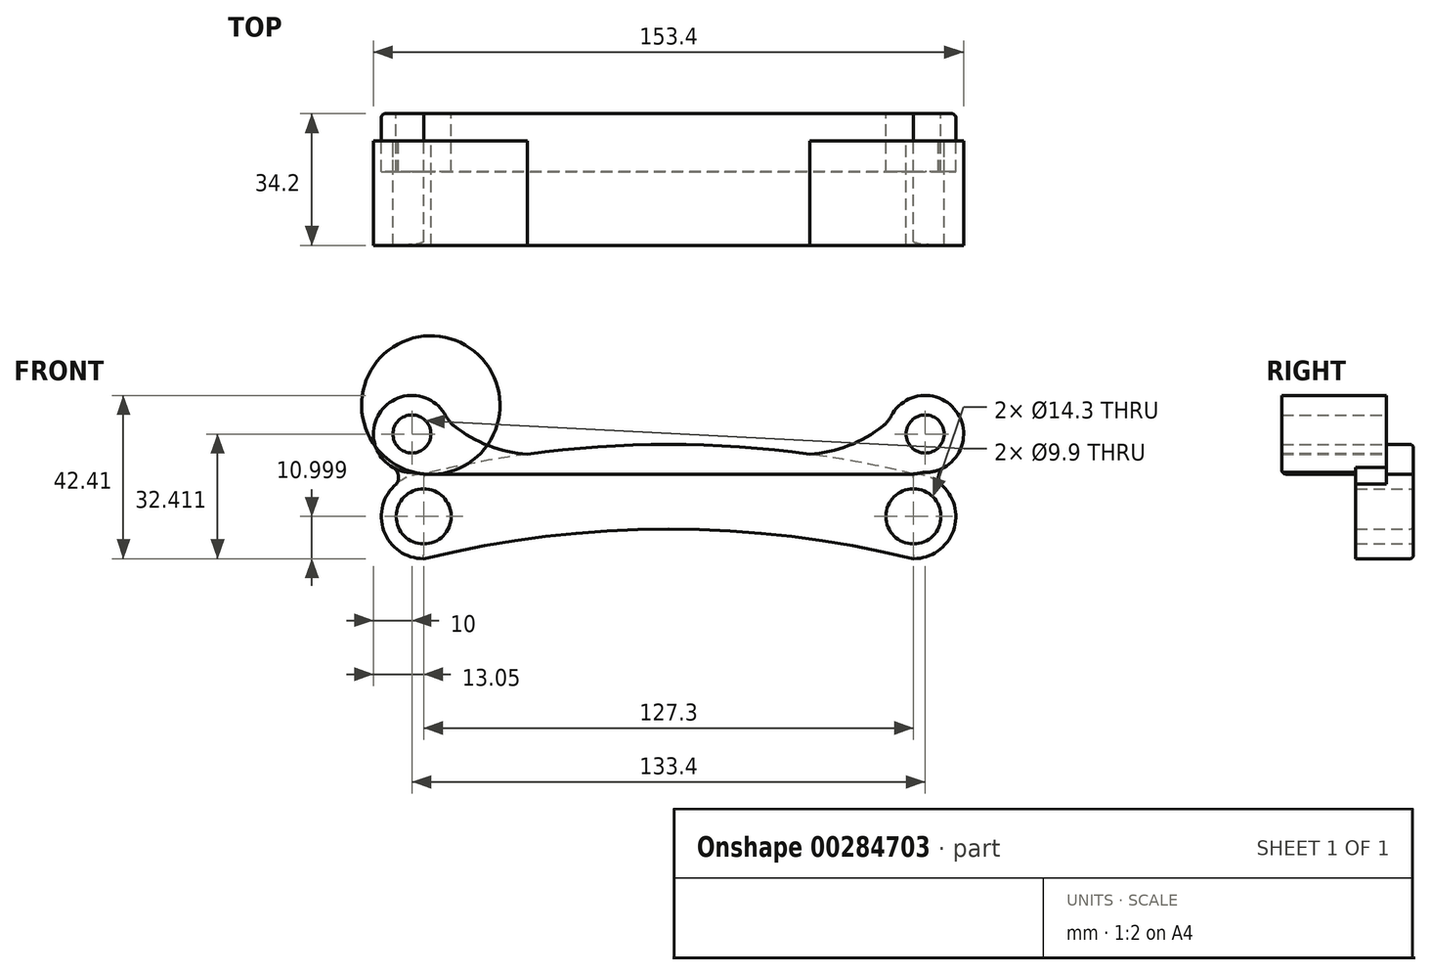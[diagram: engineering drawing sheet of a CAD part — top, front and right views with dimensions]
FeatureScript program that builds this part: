
annotation { "Feature Type Name" : "Feature", "Feature Type Description" : "" }
export const myFeature = defineFeature(function(context is Context, id is Id, definition is map)
    precondition{}
    {
        {
            var Q0;
            Q0=qCreatedBy(makeId("Front.planeOp"),FACE);
            var sketch = newSketch(context, id + "F0", { "sketchPlane" : qUnion([Q0])});
            skCircle(sketch, "E0", {"center": v(0, 0) * mm, "radius": 103 * mm, "construction": true});
            skCircle(sketch, "E1", {"center": v(0, 0) * mm, "radius": 122.2 * mm, "construction": true});
            skPoint(sketch, "E2", {"position": v(-63.65, 80.98) * mm});
            skPoint(sketch, "E3", {"position": v(63.65, 80.98) * mm});
            skPoint(sketch, "E4", {"position": v(-66.7, 102.4) * mm});
            skPoint(sketch, "E5", {"position": v(66.7, 102.4) * mm});
            skCircle(sketch, "E6", {"center": v(-66.7, 102.4) * mm, "radius": 4.95 * mm});
            skCircle(sketch, "E7", {"center": v(66.7, 102.4) * mm, "radius": 4.95 * mm});
            skCircle(sketch, "E8", {"center": v(63.65, 80.98) * mm, "radius": 7.15 * mm});
            skCircle(sketch, "E9", {"center": v(-63.65, 80.98) * mm, "radius": 7.15 * mm});
            skLineSegment(sketch, "E10", {"start": v(-66.7, 102.4) * mm, "end": v(-66.7, 80.98) * mm, "construction": true});
            skPoint(sketch, "E11", {"position": v(0, 91.69) * mm});
            skPoint(sketch, "E11.positionSnap0", {"position": v(-66.7, 91.69) * mm});
            skPoint(sketch, "E12", {"position": v(-66.7, 114.19) * mm});
            skPoint(sketch, "E13", {"position": v(66.7, 114.19) * mm});
            skCircle(sketch, "E14", {"center": v(-63.65, 80.98) * mm, "radius": 11 * mm});
            skCircle(sketch, "E15", {"center": v(63.65, 80.98) * mm, "radius": 11 * mm});
            skCircle(sketch, "E16", {"center": v(-66.7, 102.4) * mm, "radius": 10 * mm});
            skCircle(sketch, "E17", {"center": v(66.7, 102.4) * mm, "radius": 10 * mm});
            skPoint(sketch, "E18", {"position": v(-63.65, 91.98) * mm});
            skPoint(sketch, "E19", {"position": v(63.65, 92.87) * mm});
            skPoint(sketch, "E20", {"position": v(63.65, 91.98) * mm});
            skPoint(sketch, "E21", {"position": v(0, 99.69) * mm});
            skArc(sketch, "E22", {"start": v(63.65, 91.98) * mm, "mid": v(0, 99.69) * mm, "end": v(-63.65, 91.98) * mm});
            skPoint(sketch, "E23", {"position": v(0, 77.69) * mm});
            skPoint(sketch, "E24", {"position": v(-63.65, 69.98) * mm});
            skPoint(sketch, "E25", {"position": v(63.65, 69.98) * mm});
            skArc(sketch, "E26", {"start": v(63.65, 69.98) * mm, "mid": v(0, 77.69) * mm, "end": v(-63.65, 69.98) * mm});
            skPoint(sketch, "E27", {"position": v(-36.7, 97.15) * mm});
            skLineSegment(sketch, "E28", {"start": v(-66.7, 102.4) * mm, "end": v(-57.3, 105.81) * mm, "construction": true});
            skArc(sketch, "E29", {"start": v(-57.3, 105.81) * mm, "mid": v(-47.73, 99.74) * mm, "end": v(-36.7, 97.15) * mm});
            skLineSegment(sketch, "E30", {"start": v(-66.7, 102.4) * mm, "end": v(-76.1, 98.97) * mm});
            skArc(sketch, "E31", {"start": v(-76.1, 98.97) * mm, "mid": v(-70.6, 94.19) * mm, "end": v(-63.65, 91.98) * mm});
            skLineSegment(sketch, "E32", {"start": v(0, 91.69) * mm, "end": v(0, 77.69) * mm, "construction": true});
            skArc(sketch, "E33.MirrorCS", {"start": v(57.3, 105.81) * mm, "mid": v(47.73, 99.74) * mm, "end": v(36.7, 97.15) * mm});
            skArc(sketch, "E34.MirrorCS", {"start": v(76.1, 98.97) * mm, "mid": v(70.6, 94.19) * mm, "end": v(63.65, 91.98) * mm});
            skLineSegment(sketch, "E35", {"start": v(-63.65, 91.98) * mm, "end": v(63.65, 91.98) * mm});
            skArc(sketch, "E36", {"start": v(-70.6, 89.5) * mm, "mid": v(-70.99, 92.05) * mm, "end": v(-72.42, 94.19) * mm});
            skPoint(sketch, "E36.startSnap0", {"position": v(-70.6, 94.19) * mm});
            skPoint(sketch, "E36.endSnap0", {"position": v(-70.6, 94.19) * mm});
            skArc(sketch, "E37.MirrorCS", {"start": v(70.6, 89.5) * mm, "mid": v(70.99, 92.05) * mm, "end": v(72.42, 94.19) * mm});
            skSolve(sketch);
        }
        {
            var Q0;
            Q0=makeQuery(id+"F0.imprint","IMPRINT",FACE,{"disambiguationData":[TD([[makeQuery(id+"F0.imprint","IMPRINT",EDGE,{"derivedFrom":sQuery(id+"F0.wireOp",EDGE,"E6")}),-1.0]])]});
            var Q1;
            {var subQ0=sQuery(id+"F0.wireOp",EDGE,"E29");var subQ1=sQuery(id+"F0.wireOp",EDGE,"E16");var subQ2=makeQuery(id+"F0.imprint","INTERSECT",VERTEX,{"disambiguationData":[OD(1.0)],"derivedFrom":[subQ1,subQ0]});Q1=makeQuery(id+"F0.imprint","IMPRINT",FACE,{"disambiguationData":[TD([[makeQuery(id+"F0.imprint","IMPRINT",EDGE,{"disambiguationData":[TD([[subQ2,1.0]])],"derivedFrom":subQ1}),-1.0]])]});}
            var Q2;
            {var subQ0=sQuery(id+"F0.wireOp",EDGE,"E33.MirrorCS");var subQ1=sQuery(id+"F0.wireOp",EDGE,"E17");var subQ2=makeQuery(id+"F0.imprint","INTERSECT",VERTEX,{"disambiguationData":[OD(1.0)],"derivedFrom":[subQ1,subQ0]});Q2=makeQuery(id+"F0.imprint","IMPRINT",FACE,{"disambiguationData":[TD([[makeQuery(id+"F0.imprint","IMPRINT",EDGE,{"disambiguationData":[TD([[subQ2,-1.0]])],"derivedFrom":subQ1}),-1.0]])]});}
            var Q3;
            {var subQ0=sQuery(id+"F0.wireOp",EDGE,"E35");Q3=makeQuery(id+"F0.imprint","IMPRINT",FACE,{"disambiguationData":[TD([[makeQuery(id+"F0.imprint","IMPRINT",EDGE,{"derivedFrom":subQ0}),1.0]])]});}
            var Q4;
            Q4=makeQuery(id+"F0.imprint","IMPRINT",FACE,{"disambiguationData":[TD([[makeQuery(id+"F0.imprint","IMPRINT",EDGE,{"derivedFrom":sQuery(id+"F0.wireOp",EDGE,"E7")}),-1.0]])]});
            var Q5;
            {var subQ0=sQuery(id+"F0.wireOp",EDGE,"E31");var subQ1=sQuery(id+"F0.wireOp",EDGE,"E16");var subQ2=makeQuery(id+"F0.imprint","INTERSECT",VERTEX,{"disambiguationData":[OD(0.0)],"derivedFrom":[subQ1,subQ0]});Q5=makeQuery(id+"F0.imprint","IMPRINT",FACE,{"disambiguationData":[TD([[makeQuery(id+"F0.imprint","IMPRINT",EDGE,{"disambiguationData":[TD([[subQ2,-1.0]])],"derivedFrom":subQ1}),1.0]])]});}
            var Q6;
            {var subQ0=sQuery(id+"F0.wireOp",EDGE,"E17");var subQ1=makeQuery(id+"F0.imprint","INTERSECT",VERTEX,{"derivedFrom":[subQ0,sQuery(id+"F0.wireOp",EDGE,"E37.MirrorCS")]});Q6=makeQuery(id+"F0.imprint","IMPRINT",FACE,{"disambiguationData":[TD([[makeQuery(id+"F0.imprint","IMPRINT",EDGE,{"disambiguationData":[TD([[subQ1,1.0]])],"derivedFrom":subQ0}),1.0]])]});}
            extrude(context, id + "F1", {"entities" : qUnion([Q0, Q1, Q2, Q3, Q4, Q5, Q6]), "depth" : 24.2 * mm});
        }
        {
            var Q0;
            {var subQ0=sQuery(id+"F0.wireOp",EDGE,"E35");Q0=makeQuery(id+"F0.imprint","IMPRINT",FACE,{"disambiguationData":[TD([[makeQuery(id+"F0.imprint","IMPRINT",EDGE,{"derivedFrom":subQ0}),-1.0]])]});}
            var Q1;
            Q1=makeQuery(id+"F0.imprint","IMPRINT",FACE,{"disambiguationData":[TD([[makeQuery(id+"F0.imprint","IMPRINT",EDGE,{"derivedFrom":sQuery(id+"F0.wireOp",EDGE,"E9")}),-1.0]])]});
            var Q2;
            Q2=makeQuery(id+"F0.imprint","IMPRINT",FACE,{"disambiguationData":[TD([[makeQuery(id+"F0.imprint","IMPRINT",EDGE,{"derivedFrom":sQuery(id+"F0.wireOp",EDGE,"E8")}),-1.0]])]});
            var Q3;
            {var subQ0=sQuery(id+"F0.wireOp",EDGE,"E35");Q3=makeQuery(id+"F0.imprint","IMPRINT",FACE,{"disambiguationData":[TD([[makeQuery(id+"F0.imprint","IMPRINT",EDGE,{"derivedFrom":subQ0}),1.0]])]});}
            extrude(context, id + "F2", {"entities" : qUnion([Q0, Q1, Q2, Q3]), "operationType" : NewBodyOperationType.ADD, "endBound" : BoundingType.SYMMETRIC, "depth" : 20 * mm});
        }
        {
            var Q0;
            Q0=makeQuery(id+"F2.opExtrude","CAP_FACE",FACE,{"disambiguationData":[OSD([sQuery(id+"F0.wireOp",EDGE,"E8"),sQuery(id+"F0.wireOp",EDGE,"E9"),sQuery(id+"F0.wireOp",EDGE,"E14"),sQuery(id+"F0.wireOp",EDGE,"E15"),sQuery(id+"F0.wireOp",EDGE,"E22"),sQuery(id+"F0.wireOp",EDGE,"E26")])],"isStart":false});
            var sketch = newSketch(context, id + "F3", { "sketchPlane" : qUnion([Q0])});
            skArc(sketch, "E38.0", {"start": v(63.65, 69.98) * mm, "mid": v(0, 77.69) * mm, "end": v(-63.65, 69.98) * mm});
            skArc(sketch, "E39.0", {"start": v(-63.65, 91.98) * mm, "mid": v(-74.65, 80.98) * mm, "end": v(-63.65, 69.98) * mm});
            skLineSegment(sketch, "E40.0", {"start": v(-63.65, 91.98) * mm, "end": v(63.65, 91.98) * mm});
            skArc(sketch, "E41.0", {"start": v(63.65, 69.98) * mm, "mid": v(74.65, 80.98) * mm, "end": v(63.65, 91.98) * mm});
            skSolve(sketch);
        }
        {
            var Q0;
            Q0 = qSketchRegion(id + "F3", true);
            extrude(context, id + "F4", {"entities" : qUnion([Q0]), "operationType" : NewBodyOperationType.REMOVE, "oppositeDirection" : true, "depth" : 5 * mm});
        }
        {
            var Q0;
            {var subQ0=sQuery(id+"F0.wireOp",EDGE,"E29");var subQ1=sQuery(id+"F0.wireOp",EDGE,"E22");var subQ2=sQuery(id+"F0.wireOp",EDGE,"E16");var subQ3=sQuery(id+"F0.wireOp",EDGE,"E6");var subQ4=sQuery(id+"F0.wireOp",EDGE,"E31");Q0=makeQuery(id+"F2.boolean.opBoolean","SPLIT",FACE,{"disambiguationData":[TD([makeQuery(id+"F1.opExtrude","SWEPT_FACE",FACE,{"disambiguationData":[OSD([subQ3])]})])],"derivedFrom":makeQuery(id+"F1.opExtrude","CAP_FACE",FACE,{"disambiguationData":[OSD([subQ3,sQuery(id+"F0.wireOp",EDGE,"E7"),subQ2,sQuery(id+"F0.wireOp",EDGE,"E17"),subQ1,subQ0,subQ4,sQuery(id+"F0.wireOp",EDGE,"E33.MirrorCS"),sQuery(id+"F0.wireOp",EDGE,"E34.MirrorCS"),sQuery(id+"F0.wireOp",EDGE,"E35")])],"isStart":true})});}
            var sketch = newSketch(context, id + "F5", { "sketchPlane" : qUnion([Q0])});
            skArc(sketch, "E42.0", {"start": v(57.3, 105.81) * mm, "mid": v(47.73, 99.74) * mm, "end": v(36.7, 97.15) * mm});
            skArc(sketch, "E43.0", {"start": v(57.3, 105.81) * mm, "mid": v(75.06, 107.88) * mm, "end": v(66.1, 92.4) * mm});
            skArc(sketch, "E44.0", {"start": v(66.1, 92.4) * mm, "mid": v(64.88, 92.15) * mm, "end": v(63.65, 91.98) * mm});
            skCircle(sketch, "E45.0", {"center": v(66.7, 102.4) * mm, "radius": 4.95 * mm});
            skArc(sketch, "E46.0", {"start": v(-66.1, 92.4) * mm, "mid": v(-75.06, 107.88) * mm, "end": v(-57.3, 105.81) * mm});
            skArc(sketch, "E47.0", {"start": v(-57.3, 105.81) * mm, "mid": v(-47.73, 99.74) * mm, "end": v(-36.7, 97.15) * mm});
            skArc(sketch, "E48.0", {"start": v(-66.1, 92.4) * mm, "mid": v(-64.88, 92.15) * mm, "end": v(-63.65, 91.98) * mm});
            skArc(sketch, "E49.0", {"start": v(-36.7, 97.15) * mm, "mid": v(-50.24, 94.91) * mm, "end": v(-63.65, 91.98) * mm});
            skCircle(sketch, "E50.0", {"center": v(-66.7, 102.4) * mm, "radius": 4.95 * mm});
            skArc(sketch, "E51.0", {"start": v(63.65, 91.98) * mm, "mid": v(50.24, 94.91) * mm, "end": v(36.7, 97.15) * mm});
            skSolve(sketch);
        }
        {
            var Q0;
            Q0 = qSketchRegion(id + "F5", true);
            extrude(context, id + "F6", {"entities" : qUnion([Q0]), "operationType" : NewBodyOperationType.ADD, "depth" : 3 * mm});
        }
        {
            var Q0;
            Q0=makeQuery(id+"F1.opExtrude","CAP_EDGE",EDGE,{"disambiguationData":[OSD([sQuery(id+"F0.wireOp",EDGE,"E35")])],"isStart":false});
            var Q1;
            Q1=makeQuery(id+"F2.opExtrude","CAP_EDGE",EDGE,{"disambiguationData":[OSD([sQuery(id+"F0.wireOp",EDGE,"E22")])],"isStart":true});
            var Q2;
            Q2=makeQuery(id+"F2.opExtrude","CAP_EDGE",EDGE,{"disambiguationData":[OSD([sQuery(id+"F0.wireOp",EDGE,"E26")])],"isStart":true});
            var Q3;
            Q3=makeQuery(id+"F2.opExtrude","CAP_EDGE",EDGE,{"disambiguationData":[OSD([sQuery(id+"F0.wireOp",EDGE,"E14")])],"isStart":true});
            var Q4;
            Q4=makeQuery(id+"F2.opExtrude","CAP_EDGE",EDGE,{"disambiguationData":[OSD([sQuery(id+"F0.wireOp",EDGE,"E15")])],"isStart":true});
            var Q5;
            Q5=makeQuery(id+"F4.boolean.opBoolean","COPY",EDGE,{"derivedFrom":makeQuery(id+"F4.opExtrude","CAP_EDGE",EDGE,{"disambiguationData":[OSD([sQuery(id+"F3.wireOp",EDGE,"E38.0")])],"isStart":false})});
            fillet(context, id + "F7", {"entities" : qUnion([Q0, Q1, Q2, Q3, Q4, Q5]), "radius" : 1 * mm, "tangentPropagation" : true, "allowEdgeOverflow" : false});
        }
        {
            var Q0;
            Q0=makeQuery(id+"F6.boolean.opBoolean","MERGE",EDGE,{"derivedFrom":[makeQuery(id+"F1.opExtrude","SWEPT_EDGE",EDGE,{"disambiguationData":[OSD([sQuery(id+"F0.wireOp",EDGE,"E16"),sQuery(id+"F0.wireOp",EDGE,"E29")])]}),makeQuery(id+"F6.opExtrude","SWEPT_EDGE",EDGE,{"disambiguationData":[OSD([sQuery(id+"F5.wireOp",EDGE,"E42.0"),sQuery(id+"F5.wireOp",EDGE,"E43.0")])]})]});
            var Q1;
            Q1=makeQuery(id+"F6.boolean.opBoolean","MERGE",EDGE,{"derivedFrom":[makeQuery(id+"F1.opExtrude","SWEPT_EDGE",EDGE,{"disambiguationData":[OSD([sQuery(id+"F0.wireOp",EDGE,"E17"),sQuery(id+"F0.wireOp",EDGE,"E33.MirrorCS")])]}),makeQuery(id+"F6.opExtrude","SWEPT_EDGE",EDGE,{"disambiguationData":[OSD([sQuery(id+"F5.wireOp",EDGE,"E46.0"),sQuery(id+"F5.wireOp",EDGE,"E47.0")])]})]});
            fillet(context, id + "F8", {"entities" : qUnion([Q0, Q1]), "radius" : 8 * mm, "tangentPropagation" : true, "allowEdgeOverflow" : false});
        }
        {
            var Q0;
            Q0=makeQuery(id+"F6.boolean.opBoolean","MERGE",EDGE,{"derivedFrom":[makeQuery(id+"F1.opExtrude","SWEPT_EDGE",EDGE,{"disambiguationData":[OSD([sQuery(id+"F0.wireOp",EDGE,"E16"),sQuery(id+"F0.wireOp",EDGE,"E31")])]}),makeQuery(id+"F6.opExtrude","SWEPT_EDGE",EDGE,{"disambiguationData":[OSD([sQuery(id+"F5.wireOp",EDGE,"E43.0"),sQuery(id+"F5.wireOp",EDGE,"E44.0")])]})]});
            var Q1;
            Q1=makeQuery(id+"F6.boolean.opBoolean","MERGE",EDGE,{"derivedFrom":[makeQuery(id+"F1.opExtrude","SWEPT_EDGE",EDGE,{"disambiguationData":[OSD([sQuery(id+"F0.wireOp",EDGE,"E17"),sQuery(id+"F0.wireOp",EDGE,"E34.MirrorCS")])]}),makeQuery(id+"F6.opExtrude","SWEPT_EDGE",EDGE,{"disambiguationData":[OSD([sQuery(id+"F5.wireOp",EDGE,"E46.0"),sQuery(id+"F5.wireOp",EDGE,"E48.0")])]})]});
            fillet(context, id + "F9", {"entities" : qUnion([Q0, Q1]), "radius" : 5 * mm, "tangentPropagation" : true, "allowEdgeOverflow" : false});
        }
        {
            var Q0;
            Q0=makeQuery(id+"F6.opExtrude","CAP_FACE",FACE,{"disambiguationData":[OSD([sQuery(id+"F5.wireOp",EDGE,"E46.0"),sQuery(id+"F5.wireOp",EDGE,"E47.0"),sQuery(id+"F5.wireOp",EDGE,"E48.0"),sQuery(id+"F5.wireOp",EDGE,"E49.0"),sQuery(id+"F5.wireOp",EDGE,"E50.0")])],"isStart":false});
            var sketch = newSketch(context, id + "F10", { "sketchPlane" : qUnion([Q0])});
            skArc(sketch, "E52.0", {"start": v(-66.63, 92.4) * mm, "mid": v(-75.27, 107.54) * mm, "end": v(-57.84, 107.03) * mm});
            skPoint(sketch, "E53", {"position": v(-71.65, 93.7) * mm});
            skArc(sketch, "E54.0", {"start": v(-63.65, 69.98) * mm, "mid": v(-74.65, 80.98) * mm, "end": v(-63.65, 91.98) * mm});
            skPoint(sketch, "E55", {"position": v(-71.65, 88.53) * mm});
            skArc(sketch, "E56", {"start": v(-71.65, 88.53) * mm, "mid": v(-70.17, 91.12) * mm, "end": v(-71.65, 93.7) * mm});
            skArc(sketch, "E57.0", {"start": v(-66.63, 92.4) * mm, "mid": v(-66.09, 92.37) * mm, "end": v(-65.55, 92.28) * mm});
            skArc(sketch, "E58.0", {"start": v(-65.55, 92.28) * mm, "mid": v(-64.6, 92.1) * mm, "end": v(-63.65, 91.98) * mm});
            skLineSegment(sketch, "E59", {"start": v(0, 0) * mm, "end": v(0, 113) * mm, "construction": true});
            skArc(sketch, "E60.MirrorCS", {"start": v(71.65, 88.53) * mm, "mid": v(70.17, 91.12) * mm, "end": v(71.65, 93.7) * mm});
            skArc(sketch, "E61.MirrorCS", {"start": v(66.63, 92.4) * mm, "mid": v(75.27, 107.54) * mm, "end": v(57.84, 107.03) * mm});
            skArc(sketch, "E62.MirrorCS", {"start": v(66.63, 92.4) * mm, "mid": v(66.09, 92.37) * mm, "end": v(65.55, 92.28) * mm});
            skArc(sketch, "E63.MirrorCS", {"start": v(65.55, 92.28) * mm, "mid": v(64.6, 92.1) * mm, "end": v(63.65, 91.98) * mm});
            skArc(sketch, "E64.MirrorCS", {"start": v(63.65, 69.98) * mm, "mid": v(74.65, 80.98) * mm, "end": v(63.65, 91.98) * mm});
            skSolve(sketch);
        }
        {
            var Q0;
            Q0 = qSketchRegion(id + "F10", true);
            extrude(context, id + "F11", {"entities" : qUnion([Q0]), "operationType" : NewBodyOperationType.ADD, "oppositeDirection" : true, "depth" : 8 * mm});
        }
    });
